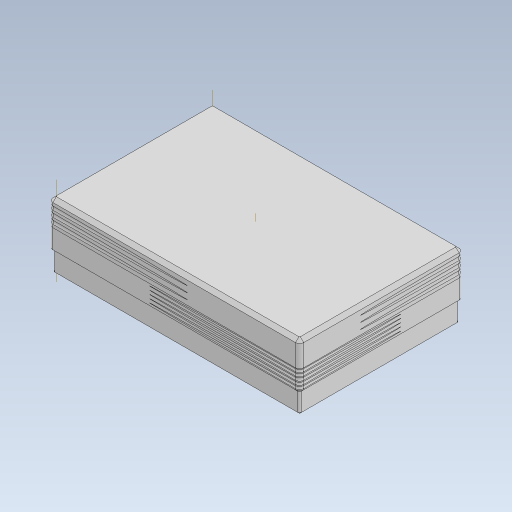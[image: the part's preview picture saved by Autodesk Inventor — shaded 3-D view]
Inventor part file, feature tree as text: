
AUTODESK INVENTOR PART (.ipt)
format: ipt  version: 2023 (Build 270158030, 158C)  size: 515,072 bytes
history: native  units: mm
features: projected_geometry x28, sketch x12, extrude x11, chamfer x5, other x4, plane x2, revolve x2, pattern_circular x2, fillet x1
ambient origin geometry x8: Origin, YZ Plane, XZ Plane, XY Plane, X Axis, Y Axis, Z Axis, Center Point
bodies: Solid1 (feature_tree)
feature tree (67):
  extrude  "Extrusion1"  Depth=112.0mm
  extrude  "Extrusion2"  Depth=88.0mm
  extrude  "Extrusion3"  Depth=45.0mm
  fillet  "Fillet1"  Radius=2.0mm
  extrude  "Extrusion4"  Depth=3.0mm
  extrude  "Extrusion5"  Depth=1.5mm TaperAngle=45.0deg
  chamfer  "Chamfer1"  Distance=15.0mm
  chamfer  "Chamfer2"  Distance=1.5mm Angle=45.0deg
  chamfer  "Chamfer3"  Distance=1.0mm Angle=45.0deg
  extrude  "Extrusion6"  Depth=16.5mm TaperAngle=0.0deg
  extrude  "Extrusion7"  Depth=2.5mm TaperAngle=45.0deg
  chamfer  "Chamfer4"  Distance=4.5mm
  chamfer  "Chamfer5"  Distance=5.0mm
  other  "Work Axis1"
  plane  "Work Plane1"
  revolve  "Revolution1"  [1 undecoded]
  extrude  "Extrusion8"  TaperAngle=90.0deg  [1 undecoded]
  extrude  "Extrusion9"  Depth=3.0mm
  pattern_circular  "Circular Pattern1"  [2 undecoded]
  other  "Work Axis2"
  plane  "Work Plane2"
  revolve  "Revolution2"  Angle=360.0deg
  extrude  "Extrusion10"  Depth=3.0mm
  extrude  "Extrusion11"  Depth=3.0mm
  pattern_circular  "Circular Pattern2"  [2 undecoded]
  sketch  "Sketch1"  dims[d0=176.0mm d1=112.0mm]
  sketch  "Sketch2"  dims[d2=56.0mm d3=88.0mm]
  projected_geometry  "Projected Loop1"
  sketch  "Sketch3"  dims[d4=45.0mm d5=0.0mm d6=4.0mm d7=2.0mm d8=0.0mm]
  other  "box"
  sketch  "Sketch4"  dims[d10=45.0mm d11=0.0mm d12=3.0mm]
  projected_geometry  "Projected Loop5"
  projected_geometry  "Projected Loop6"
  projected_geometry  "Projected Loop7"
  sketch  "Sketch6"  dims[d14=15.0mm d15=0.0mm d16=1.5mm d17=2.0mm d18=45.0deg d19=15.0mm d20=0.0mm]
  projected_geometry  "Projected Loop8"
  projected_geometry  "Projected Loop9"
  projected_geometry  "Projected Loop10"
  projected_geometry  "Projected Loop11"
  projected_geometry  "Projected Loop12"
  projected_geometry  "Projected Loop13"
  projected_geometry  "Projected Loop14"
  projected_geometry  "Projected Loop15"
  other  "lid"
  sketch  "Sketch7"  dims[d21=1.0mm]
  projected_geometry  "Projected Loop16"
  sketch  "Sketch8"  dims[d24=1.5mm]
  sketch  "Sketch9"  dims[d25=1.5mm d26=1.5mm d27=2.0mm d28=45.0deg d29=1.0mm d30=2.0mm d31=45.0deg]
  projected_geometry  "Projected Loop17"
  projected_geometry  "Projected Loop18"
  projected_geometry  "Projected Loop19"
  sketch  "Sketch10"  dims[d32=2.0mm d33=0.0mm d34=16.5mm d35=0.0mm]
  projected_geometry  "Projected Loop20"
  projected_geometry  "Projected Loop21"
  projected_geometry  "Projected Loop22"
  sketch  "Sketch11"  dims[d36=1.5mm d37=2.0mm d38=45.0deg d39=2.5mm d40=2.0mm d41=45.0deg]
  sketch  "Sketch12"  dims[d42=3.5mm]
  projected_geometry  "Projected Loop23"
  projected_geometry  "Projected Loop24"
  projected_geometry  "Projected Loop25"
  projected_geometry  "Projected Loop26"
  projected_geometry  "Projected Loop27"
  sketch  "Sketch13"  dims[d43=4.5mm d44=4.5mm d45=5.0mm d46=3.0mm d47=90.0deg d48=3.0mm d49=-0.038397mm d50=0.0mm d51=-0.05236mm d52=20.0mm d53=360.0deg d55=1.5mm d56=2.7mm d57=2.7mm d58=2.7mm d59=2.7mm d60=2.0mm d61=90.0deg d62=4.304mm d63=-0.034907mm d64=19.689mm d65=-0.05236mm d66=20.0mm d67=360.0deg]
  projected_geometry  "Projected Loop28"
  projected_geometry  "Projected Loop29"
  projected_geometry  "Projected Loop30"
  projected_geometry  "Projected Loop31"
note: 6 required parameter values undecoded (feature->parameter linkage not recoverable at this tier; creation-order binding heuristic only, values carry confidence <= 0.55)